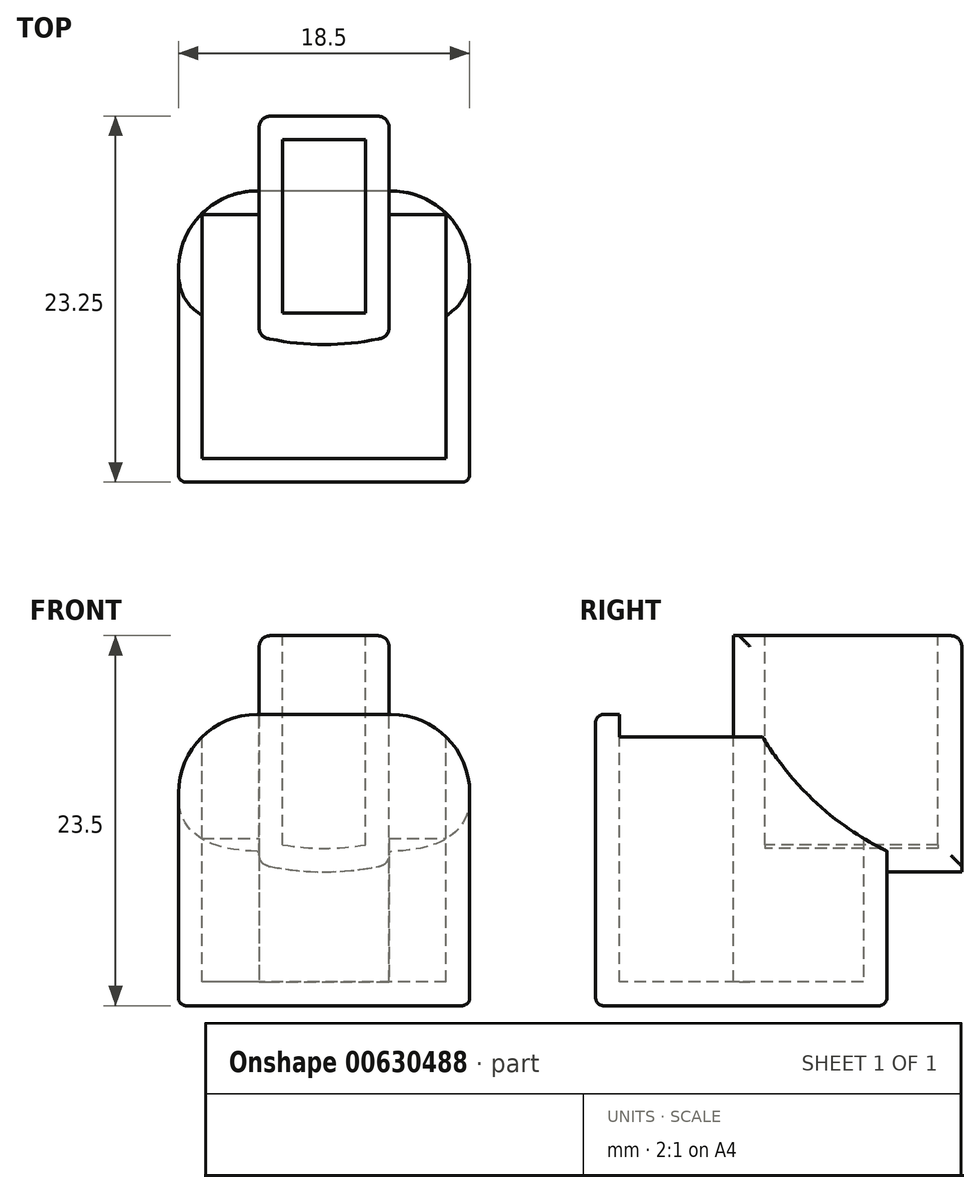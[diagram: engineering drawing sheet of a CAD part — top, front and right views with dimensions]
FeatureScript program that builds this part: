
annotation { "Feature Type Name" : "Feature", "Feature Type Description" : "" }
export const myFeature = defineFeature(function(context is Context, id is Id, definition is map)
    precondition{}
    {
        {
            var Q0;
            Q0=qCreatedBy(makeId("Top.planeOp"),FACE);
            var sketch = newSketch(context, id + "F0", { "sketchPlane" : qUnion([Q0])});
            skLineSegment(sketch, "E0.rect.bottom", {"start": v(9.25, 9.25) * mm, "end": v(-9.25, 9.25) * mm});
            skLineSegment(sketch, "E0.rect.top", {"start": v(9.25, -9.25) * mm, "end": v(-9.25, -9.25) * mm});
            skLineSegment(sketch, "E0.rect.left", {"start": v(9.25, 9.25) * mm, "end": v(9.25, -9.25) * mm});
            skLineSegment(sketch, "E0.rect.right", {"start": v(-9.25, 9.25) * mm, "end": v(-9.25, -9.25) * mm});
            skPoint(sketch, "E0.rect.middle", {"position": v(0, 0) * mm});
            skSolve(sketch);
        }
        {
            var Q0;
            Q0=makeQuery(id+"F0.imprint","IMPRINT",FACE,{"disambiguationData":[TD([[makeQuery(id+"F0.imprint","IMPRINT",EDGE,{"derivedFrom":sQuery(id+"F0.wireOp",EDGE,"E0.rect.bottom")}),1.0]])]});
            extrude(context, id + "F1", {"entities" : qUnion([Q0]), "oppositeDirection" : true, "depth" : 18.5 * mm});
        }
        {
            var Q0;
            Q0=makeQuery(id+"F1.opExtrude","SWEPT_FACE",FACE,{"disambiguationData":[OSD([sQuery(id+"F0.wireOp",EDGE,"E0.rect.left")])]});
            var sketch = newSketch(context, id + "F2", { "sketchPlane" : qUnion([Q0])});
            skPoint(sketch, "E1", {"position": v(2, 0) * mm});
            skPoint(sketch, "E2", {"position": v(-9.25, -18.5) * mm});
            skPoint(sketch, "E3", {"position": v(4.19, -5.06) * mm});
            skCircle(sketch, "E4", {"center": v(17.62, 8.37) * mm, "radius": 19 * mm});
            skSolve(sketch);
        }
        {
            var Q0;
            Q0=qSketchRegion(id+"F2",true);
            extrude(context, id + "F3", {"entities" : qUnion([Q0]), "operationType" : NewBodyOperationType.REMOVE, "oppositeDirection" : true, "depth" : 25.4 * mm});
        }
        {
            var Q0;
            Q0=makeQuery(id+"F1.opExtrude","CAP_FACE",FACE,{"disambiguationData":[OSD([sQuery(id+"F0.wireOp",EDGE,"E0.rect.bottom"),sQuery(id+"F0.wireOp",EDGE,"E0.rect.top"),sQuery(id+"F0.wireOp",EDGE,"E0.rect.left"),sQuery(id+"F0.wireOp",EDGE,"E0.rect.right")])],"isStart":true});
            var Q1;
            Q1=makeQuery(id+"F3.boolean.opBoolean","COPY",FACE,{"derivedFrom":makeQuery(id+"F3.opExtrude","SWEPT_FACE",FACE,{"disambiguationData":[OSD([sQuery(id+"F2.wireOp",EDGE,"E4")])]})});
            shell(context, id + "F4", {"entities" : qUnion([Q0, Q1]), "thickness" : 1.5 * mm});
        }
        {
            var Q0;
            Q0=qCreatedBy(makeId("Front.planeOp"),FACE);
            var sketch = newSketch(context, id + "F5", { "sketchPlane" : qUnion([Q0])});
            skPoint(sketch, "E5", {"position": v(0, 5) * mm});
            skLineSegment(sketch, "E6", {"start": v(0, 5) * mm, "end": v(0, -9.5) * mm});
            skLineSegment(sketch, "E7.top", {"start": v(4.12, 5) * mm, "end": v(-4.12, 5) * mm});
            skLineSegment(sketch, "E7.left", {"start": v(4.12, -9.5) * mm, "end": v(4.12, 5) * mm});
            skLineSegment(sketch, "E7.right", {"start": v(-4.12, -9.5) * mm, "end": v(-4.12, 5) * mm});
            skPoint(sketch, "E8", {"position": v(0, -10) * mm});
            skArc(sketch, "E9", {"start": v(-4.12, -9.5) * mm, "mid": v(0, -10) * mm, "end": v(4.13, -9.5) * mm});
            skSolve(sketch);
        }
        {
            var Q0;
            Q0=qSketchRegion(id+"F5",true);
            extrude(context, id + "F6", {"entities" : qUnion([Q0]), "operationType" : NewBodyOperationType.ADD, "oppositeDirection" : true, "depth" : 14 * mm});
        }
        {
            var Q0;
            Q0=makeQuery(id+"F6.opExtrude","SWEPT_FACE",FACE,{"disambiguationData":[OSD([sQuery(id+"F5.wireOp",EDGE,"E7.top")])]});
            shell(context, id + "F7", {"entities" : qUnion([Q0]), "thickness" : 1.5 * mm});
        }
        {
            var Q0;
            Q0=makeQuery(id+"F6.opExtrude","SWEPT_FACE",FACE,{"disambiguationData":[OSD([sQuery(id+"F5.wireOp",EDGE,"E7.top")])]});
            var sketch = newSketch(context, id + "F8", { "sketchPlane" : qUnion([Q0])});
            skArc(sketch, "E10", {"start": v(-4.13, 0) * mm, "mid": v(0, -0.5) * mm, "end": v(4.12, 0) * mm});
            skLineSegment(sketch, "E11", {"start": v(-4.13, 0) * mm, "end": v(4.12, 0) * mm});
            skSolve(sketch);
        }
        {
            var Q0;
            Q0=makeQuery(id+"F8.imprint","IMPRINT",FACE,{"disambiguationData":[TD([[makeQuery(id+"F8.imprint","IMPRINT",EDGE,{"derivedFrom":sQuery(id+"F8.wireOp",EDGE,"E10")}),1.0]])]});
            extrude(context, id + "F9", {"entities" : qUnion([Q0]), "operationType" : NewBodyOperationType.ADD, "oppositeDirection" : true, "depth" : 23.32 * mm});
        }
        {
            var Q0;
            Q0=makeQuery(id+"F9.opExtrude","SWEPT_FACE",FACE,{"disambiguationData":[OSD([sQuery(id+"F8.wireOp",EDGE,"E11")])]});
            extrude(context, id + "F10", {"entities" : qUnion([Q0]), "operationType" : NewBodyOperationType.ADD, "depth" : 8.55 * mm});
        }
        {
            var Q0;
            Q0=makeQuery(id+"F1.opExtrude","CAP_EDGE",EDGE,{"disambiguationData":[OSD([sQuery(id+"F0.wireOp",EDGE,"E0.rect.right")])],"isStart":true});
            var Q1;
            Q1=makeQuery(id+"F1.opExtrude","CAP_EDGE",EDGE,{"disambiguationData":[OSD([sQuery(id+"F0.wireOp",EDGE,"E0.rect.left")])],"isStart":true});
            var Q2;
            Q2=makeQuery(id+"F1.opExtrude","SWEPT_EDGE",EDGE,{"disambiguationData":[OSD([sQuery(id+"F0.wireOp",EDGE,"E0.rect.bottom"),sQuery(id+"F0.wireOp",EDGE,"E0.rect.left")])]});
            var Q3;
            Q3=makeQuery(id+"F1.opExtrude","SWEPT_EDGE",EDGE,{"disambiguationData":[OSD([sQuery(id+"F0.wireOp",EDGE,"E0.rect.bottom"),sQuery(id+"F0.wireOp",EDGE,"E0.rect.right")])]});
            fillet(context, id + "F11", {"entities" : qUnion([Q0, Q1, Q2, Q3]), "radius" : 5 * mm, "tangentPropagation" : true, "allowEdgeOverflow" : false});
        }
        {
            var Q0;
            Q0=makeQuery(id+"F6.opExtrude","CAP_EDGE",EDGE,{"disambiguationData":[OSD([sQuery(id+"F5.wireOp",EDGE,"E7.left")])],"isStart":false});
            var Q1;
            Q1=makeQuery(id+"F6.opExtrude","CAP_EDGE",EDGE,{"disambiguationData":[OSD([sQuery(id+"F5.wireOp",EDGE,"E7.right")])],"isStart":false});
            var Q2;
            Q2=makeQuery(id+"F6.opExtrude","SWEPT_EDGE",EDGE,{"disambiguationData":[OSD([sQuery(id+"F5.wireOp",EDGE,"E7.top"),sQuery(id+"F5.wireOp",EDGE,"E7.left")])]});
            var Q3;
            Q3=makeQuery(id+"F6.opExtrude","SWEPT_EDGE",EDGE,{"disambiguationData":[OSD([sQuery(id+"F5.wireOp",EDGE,"E7.top"),sQuery(id+"F5.wireOp",EDGE,"E7.right")])]});
            var Q4;
            {var subQ0=sQuery(id+"F5.wireOp",EDGE,"E9");var subQ1=sQuery(id+"F5.wireOp",EDGE,"E7.right");Q4=makeQuery(id+"F6.boolean.opBoolean","SPLIT",EDGE,{"disambiguationData":[TD([makeQuery(id+"F1.opExtrude","SWEPT_FACE",FACE,{"disambiguationData":[OSD([sQuery(id+"F0.wireOp",EDGE,"E0.rect.bottom")])]})])],"derivedFrom":makeQuery(id+"F6.opExtrude","SWEPT_EDGE",EDGE,{"disambiguationData":[OSD([subQ1,subQ0])]})});}
            var Q5;
            {var subQ0=sQuery(id+"F5.wireOp",EDGE,"E9");var subQ1=sQuery(id+"F5.wireOp",EDGE,"E7.left");Q5=makeQuery(id+"F6.boolean.opBoolean","SPLIT",EDGE,{"disambiguationData":[TD([makeQuery(id+"F1.opExtrude","SWEPT_FACE",FACE,{"disambiguationData":[OSD([sQuery(id+"F0.wireOp",EDGE,"E0.rect.bottom")])]})])],"derivedFrom":makeQuery(id+"F6.opExtrude","SWEPT_EDGE",EDGE,{"disambiguationData":[OSD([subQ1,subQ0])]})});}
            var Q6;
            {var subQ0=sQuery(id+"F8.wireOp",EDGE,"E11");var subQ1=sQuery(id+"F8.wireOp",EDGE,"E10");var subQ2=sQuery(id+"F5.wireOp",EDGE,"E7.left");var subQ3=sQuery(id+"F5.wireOp",EDGE,"E7.top");var subQ4=makeQuery(id+"F9.opExtrude","SWEPT_EDGE",EDGE,{"disambiguationData":[OSD([subQ3,subQ2,subQ1,subQ0])]});Q6=makeQuery(id+"F10.boolean.opBoolean","MERGE",EDGE,{"derivedFrom":[makeQuery(id+"F9.boolean.opBoolean","MERGE",EDGE,{"derivedFrom":[makeQuery(id+"F6.opExtrude","CAP_EDGE",EDGE,{"disambiguationData":[OSD([subQ2])],"isStart":true}),subQ4]}),makeQuery(id+"F9.boolean.opBoolean","SPLIT",EDGE,{"derivedFrom":subQ4}),makeQuery(id+"F10.opExtrude","CAP_EDGE",EDGE,{"disambiguationData":[OSD([subQ3,subQ2,subQ1,subQ0])],"isStart":true})]});}
            var Q7;
            {var subQ0=sQuery(id+"F8.wireOp",EDGE,"E11");var subQ1=sQuery(id+"F8.wireOp",EDGE,"E10");var subQ2=sQuery(id+"F5.wireOp",EDGE,"E7.right");var subQ3=sQuery(id+"F5.wireOp",EDGE,"E7.top");var subQ4=makeQuery(id+"F9.opExtrude","SWEPT_EDGE",EDGE,{"disambiguationData":[OSD([subQ3,subQ2,subQ1,subQ0])]});Q7=makeQuery(id+"F10.boolean.opBoolean","MERGE",EDGE,{"derivedFrom":[makeQuery(id+"F9.boolean.opBoolean","MERGE",EDGE,{"derivedFrom":[makeQuery(id+"F6.opExtrude","CAP_EDGE",EDGE,{"disambiguationData":[OSD([subQ2])],"isStart":true}),subQ4]}),makeQuery(id+"F9.boolean.opBoolean","SPLIT",EDGE,{"derivedFrom":subQ4}),makeQuery(id+"F10.opExtrude","CAP_EDGE",EDGE,{"disambiguationData":[OSD([subQ3,subQ2,subQ1,subQ0])],"isStart":true})]});}
            var Q8;
            Q8=makeQuery(id+"F6.opExtrude","CAP_EDGE",EDGE,{"disambiguationData":[OSD([sQuery(id+"F5.wireOp",EDGE,"E7.top")])],"isStart":false});
            fillet(context, id + "F12", {"entities" : qUnion([Q0, Q1, Q2, Q3, Q4, Q5, Q6, Q7, Q8]), "radius" : 0.7 * mm, "tangentPropagation" : true, "allowEdgeOverflow" : false});
        }
        {
            var Q0;
            Q0=makeQuery(id+"F1.opExtrude","CAP_EDGE",EDGE,{"disambiguationData":[OSD([sQuery(id+"F0.wireOp",EDGE,"E0.rect.left")])],"isStart":false});
            var Q1;
            Q1=makeQuery(id+"F1.opExtrude","CAP_EDGE",EDGE,{"disambiguationData":[OSD([sQuery(id+"F0.wireOp",EDGE,"E0.rect.top")])],"isStart":false});
            var Q2;
            Q2=makeQuery(id+"F1.opExtrude","SWEPT_EDGE",EDGE,{"disambiguationData":[OSD([sQuery(id+"F0.wireOp",EDGE,"E0.rect.top"),sQuery(id+"F0.wireOp",EDGE,"E0.rect.left")])]});
            var Q3;
            Q3=makeQuery(id+"F1.opExtrude","CAP_EDGE",EDGE,{"disambiguationData":[OSD([sQuery(id+"F0.wireOp",EDGE,"E0.rect.right")])],"isStart":false});
            var Q4;
            Q4=makeQuery(id+"F1.opExtrude","SWEPT_EDGE",EDGE,{"disambiguationData":[OSD([sQuery(id+"F0.wireOp",EDGE,"E0.rect.top"),sQuery(id+"F0.wireOp",EDGE,"E0.rect.right")])]});
            fillet(context, id + "F13", {"entities" : qUnion([Q0, Q1, Q2, Q3, Q4]), "radius" : 0.5 * mm, "tangentPropagation" : true, "allowEdgeOverflow" : false});
        }
    });
